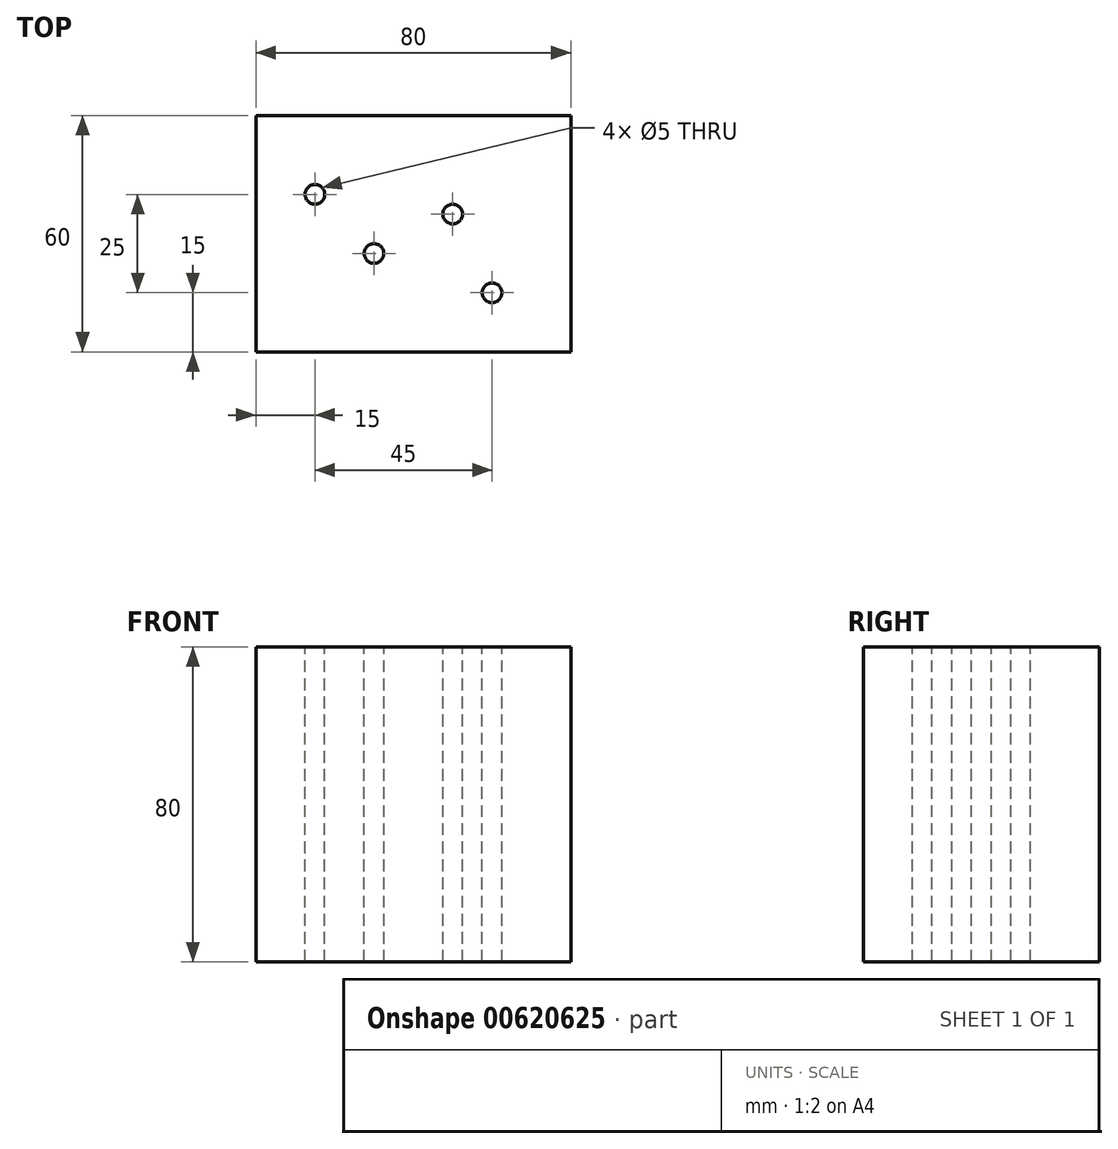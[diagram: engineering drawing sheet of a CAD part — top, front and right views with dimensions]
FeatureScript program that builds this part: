
annotation { "Feature Type Name" : "Feature", "Feature Type Description" : "" }
export const myFeature = defineFeature(function(context is Context, id is Id, definition is map)
    precondition{}
    {
        {
            var Q0;
            Q0=qCreatedBy(makeId("Top.planeOp"),FACE);
            var sketch = newSketch(context, id + "F0", { "sketchPlane" : qUnion([Q0])});
            skLineSegment(sketch, "E0.bottom", {"start": v(0, 0) * mm, "end": v(80, 0) * mm});
            skLineSegment(sketch, "E0.top", {"start": v(0, 60) * mm, "end": v(80, 60) * mm});
            skLineSegment(sketch, "E0.left", {"start": v(0, 0) * mm, "end": v(0, 60) * mm});
            skLineSegment(sketch, "E0.right", {"start": v(80, 0) * mm, "end": v(80, 60) * mm});
            skSolve(sketch);
        }
        {
            var Q0;
            Q0 = qSketchRegion(id + "F0", true);
            extrude(context, id + "F1", {"entities" : qUnion([Q0]), "depth" : 80 * mm, "offsetDistance" : 25 * mm});
        }
        {
            var Q0;
            Q0=makeQuery(id+"F1.opExtrude","CAP_FACE",FACE,{"disambiguationData":[OSD([sQuery(id+"F0.wireOp",EDGE,"E0.bottom"),sQuery(id+"F0.wireOp",EDGE,"E0.top"),sQuery(id+"F0.wireOp",EDGE,"E0.left"),sQuery(id+"F0.wireOp",EDGE,"E0.right")])],"isStart":false});
            var sketch = newSketch(context, id + "F2", { "sketchPlane" : qUnion([Q0])});
            skPoint(sketch, "E1", {"position": v(30, 24.98) * mm});
            skPoint(sketch, "E2", {"position": v(50, 35) * mm});
            skPoint(sketch, "E3", {"position": v(60, 15) * mm});
            skPoint(sketch, "E4", {"position": v(15, 40) * mm});
            skSolve(sketch);
        }
        {
            var Q0;
            Q0=sQuery(id+"F2.wireOp",VERTEX,"E4");
            var Q1;
            Q1=sQuery(id+"F2.wireOp",VERTEX,"E1");
            var Q2;
            Q2=sQuery(id+"F2.wireOp",VERTEX,"E3");
            var Q3;
            Q3=sQuery(id+"F2.wireOp",VERTEX,"E2");
            var Q4;
            Q4=makeQuery(id+"F1.opExtrude","SWEPT_BODY",BODY,{"disambiguationData":[OSD([sQuery(id+"F0.wireOp",EDGE,"E0.bottom"),sQuery(id+"F0.wireOp",EDGE,"E0.top"),sQuery(id+"F0.wireOp",EDGE,"E0.left"),sQuery(id+"F0.wireOp",EDGE,"E0.right")])]});
            hole(context, id + "F3", {"style" : HoleStyle.SIMPLE, "endStyle" : HoleEndStyle.THROUGH, "holeDiameter" : 5 * mm, "majorDiameter" : 5 * mm, "isTappedThrough" : true, "tappedDepth" : 12 * mm, "tapClearance" : 3, "locations" : qUnion([Q0, Q1, Q2, Q3]), "scope" : qUnion([Q4])});
        }
    });
